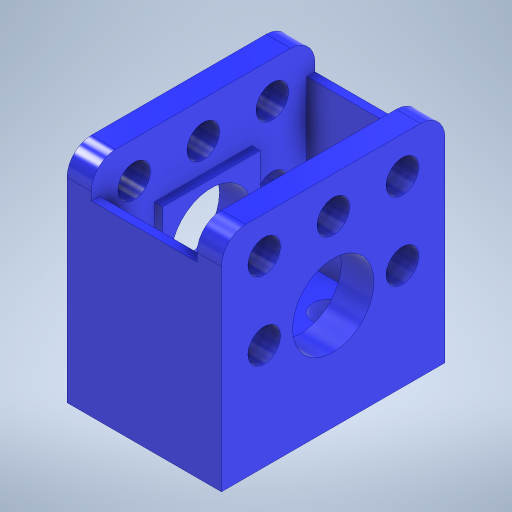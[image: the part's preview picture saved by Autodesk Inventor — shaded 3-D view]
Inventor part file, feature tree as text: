
AUTODESK INVENTOR PART (.ipt)
format: ipt  version: 2023.1 (Build 271208000, 208)  size: 364,544 bytes
history: native  units: mm
features: sketch x8, extrude x7, fillet x1, hole x1
ambient origin geometry x8: Origin, YZ Plane, XZ Plane, XY Plane, X Axis, Y Axis, Z Axis, Center Point
bodies: Solid1 (feature_tree)
feature tree (17):
  extrude  "Extrusion1"  Depth=27.5mm
  extrude  "Extrusion2"  Depth=9.5mm
  extrude  "Extrusion3"  Depth=3.0mm
  fillet  "Fillet1"  Radius=3.0mm
  extrude  "Extrusion4"  Depth=1.0mm
  hole  "Hole1"  [1 undecoded]
  extrude  "Extrusion5"  Depth=3.0mm
  extrude  "Extrusion6"  Depth=4.0mm
  extrude  "Extrusion7"  Depth=9.0mm
  sketch  "Sketch1"  dims[d0=19.0mm d1=27.5mm]
  sketch  "Sketch2"  dims[d2=13.75mm d3=9.5mm]
  sketch  "Sketch3"  dims[d4=27.0mm d5=0.0mm d6=3.0mm d7=3.0mm]
  sketch  "Sketch4"  dims[d8=1.0mm d9=1.0mm]
  sketch  "Sketch5"  dims[d10=24.0mm d11=0.0mm d12=4.0mm]
  sketch  "Sketch6"  dims[d13=30.0mm d14=0.0mm d15=3.0mm]
  sketch  "Sketch7"  dims[d16=4.0mm d17=4.0mm]
  sketch  "Sketch8"  dims[d18=4.0mm d19=9.0mm d20=9.0mm d21=5.0mm d22=0.0mm d23=14.0mm d24=27.5mm d25=13.75mm d26=4.0mm d27=0.0mm d28=0.0mm d29=4.0mm d30=4.0mm d31=8.5mm d32=8.5mm d35=4.75mm d36=4.0mm d37=6.0mm d38=4.0mm d39=2.0mm d40=90.0deg d41=8.0mm d42=20.594885mm d43=12.0mm d44=12.0mm d45=6.0mm d46=6.0mm d47=1.0mm d48=0.0mm d49=1.0mm d50=0.0mm d51=10.0mm d52=0.0mm d53=0.0mm]
note: 1 required parameter value undecoded (feature->parameter linkage not recoverable at this tier; creation-order binding heuristic only, values carry confidence <= 0.55)
